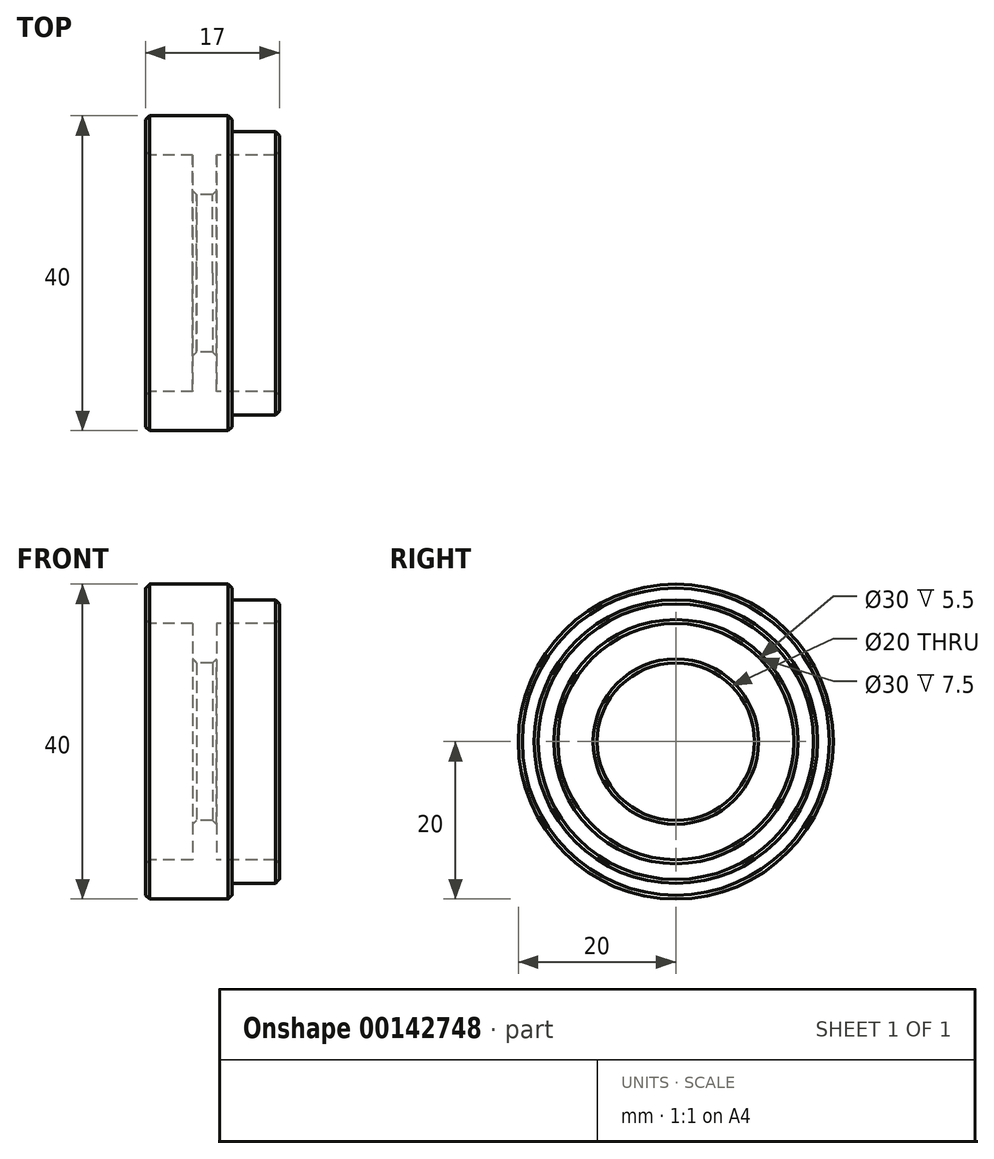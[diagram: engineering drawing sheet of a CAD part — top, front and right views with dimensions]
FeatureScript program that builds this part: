
annotation { "Feature Type Name" : "Feature", "Feature Type Description" : "" }
export const myFeature = defineFeature(function(context is Context, id is Id, definition is map)
    precondition{}
    {
        {
            var Q0;
            Q0=qCreatedBy(makeId("Top.planeOp"),FACE);
            var sketch = newSketch(context, id + "F0", { "sketchPlane" : qUnion([Q0])});
            skLineSegment(sketch, "E0", {"start": v(0, 15) * mm, "end": v(0, 20) * mm});
            skLineSegment(sketch, "E1", {"start": v(0, 0) * mm, "end": v(17, 0) * mm, "construction": true});
            skLineSegment(sketch, "E2", {"start": v(17, 0) * mm, "end": v(17, -0.91) * mm, "construction": true});
            skLineSegment(sketch, "E3", {"start": v(0, 20) * mm, "end": v(11, 20) * mm});
            skLineSegment(sketch, "E4", {"start": v(11, 20) * mm, "end": v(11, 18) * mm});
            skLineSegment(sketch, "E5", {"start": v(11, 18) * mm, "end": v(17, 18) * mm});
            skLineSegment(sketch, "E6", {"start": v(17, 18) * mm, "end": v(17, 15) * mm});
            skLineSegment(sketch, "E7", {"start": v(17, 15) * mm, "end": v(9, 15) * mm});
            skLineSegment(sketch, "E8", {"start": v(9, 15) * mm, "end": v(9, 10) * mm});
            skLineSegment(sketch, "E9", {"start": v(9, 10) * mm, "end": v(6, 10) * mm});
            skLineSegment(sketch, "E10", {"start": v(6, 10) * mm, "end": v(6, 15) * mm});
            skLineSegment(sketch, "E11", {"start": v(6, 15) * mm, "end": v(0, 15) * mm});
            skSolve(sketch);
        }
        {
            var Q0;
            Q0 = qSketchRegion(id + "F0", true);
            var Q1;
            Q1=sQuery(id+"F0.wireOp",EDGE,"E1");
            revolve(context, id + "F1", {"entities" : qUnion([Q0]), "axis" : qUnion([Q1]), "revolveType" : RevolveType.FULL});
        }
        {
            var Q0;
            Q0=makeQuery(id+"F1.opRevolve","SWEPT_EDGE",EDGE,{"disambiguationData":[OSD([sQuery(id+"F0.wireOp",EDGE,"E0"),sQuery(id+"F0.wireOp",EDGE,"E3")])]});
            var Q1;
            Q1=makeQuery(id+"F1.opRevolve","SWEPT_EDGE",EDGE,{"disambiguationData":[OSD([sQuery(id+"F0.wireOp",EDGE,"E3"),sQuery(id+"F0.wireOp",EDGE,"E4")])]});
            var Q2;
            Q2=makeQuery(id+"F1.opRevolve","SWEPT_EDGE",EDGE,{"disambiguationData":[OSD([sQuery(id+"F0.wireOp",EDGE,"E5"),sQuery(id+"F0.wireOp",EDGE,"E6")])]});
            var Q3;
            Q3=makeQuery(id+"F1.opRevolve","SWEPT_EDGE",EDGE,{"disambiguationData":[OSD([sQuery(id+"F0.wireOp",EDGE,"E0"),sQuery(id+"F0.wireOp",EDGE,"E11")])]});
            var Q4;
            Q4=makeQuery(id+"F1.opRevolve","SWEPT_EDGE",EDGE,{"disambiguationData":[OSD([sQuery(id+"F0.wireOp",EDGE,"E9"),sQuery(id+"F0.wireOp",EDGE,"E10")])]});
            var Q5;
            Q5=makeQuery(id+"F1.opRevolve","SWEPT_EDGE",EDGE,{"disambiguationData":[OSD([sQuery(id+"F0.wireOp",EDGE,"E8"),sQuery(id+"F0.wireOp",EDGE,"E9")])]});
            var Q6;
            Q6=makeQuery(id+"F1.opRevolve","SWEPT_EDGE",EDGE,{"disambiguationData":[OSD([sQuery(id+"F0.wireOp",EDGE,"E6"),sQuery(id+"F0.wireOp",EDGE,"E7")])]});
            chamfer(context, id + "F2", {"entities" : qUnion([Q0, Q1, Q2, Q3, Q4, Q5, Q6]), "chamferType" : ChamferType.OFFSET_ANGLE, "width" : 0.5 * mm, "oppositeDirection" : false, "angle" : 45 * degree, "tangentPropagation" : true});
        }
    });
